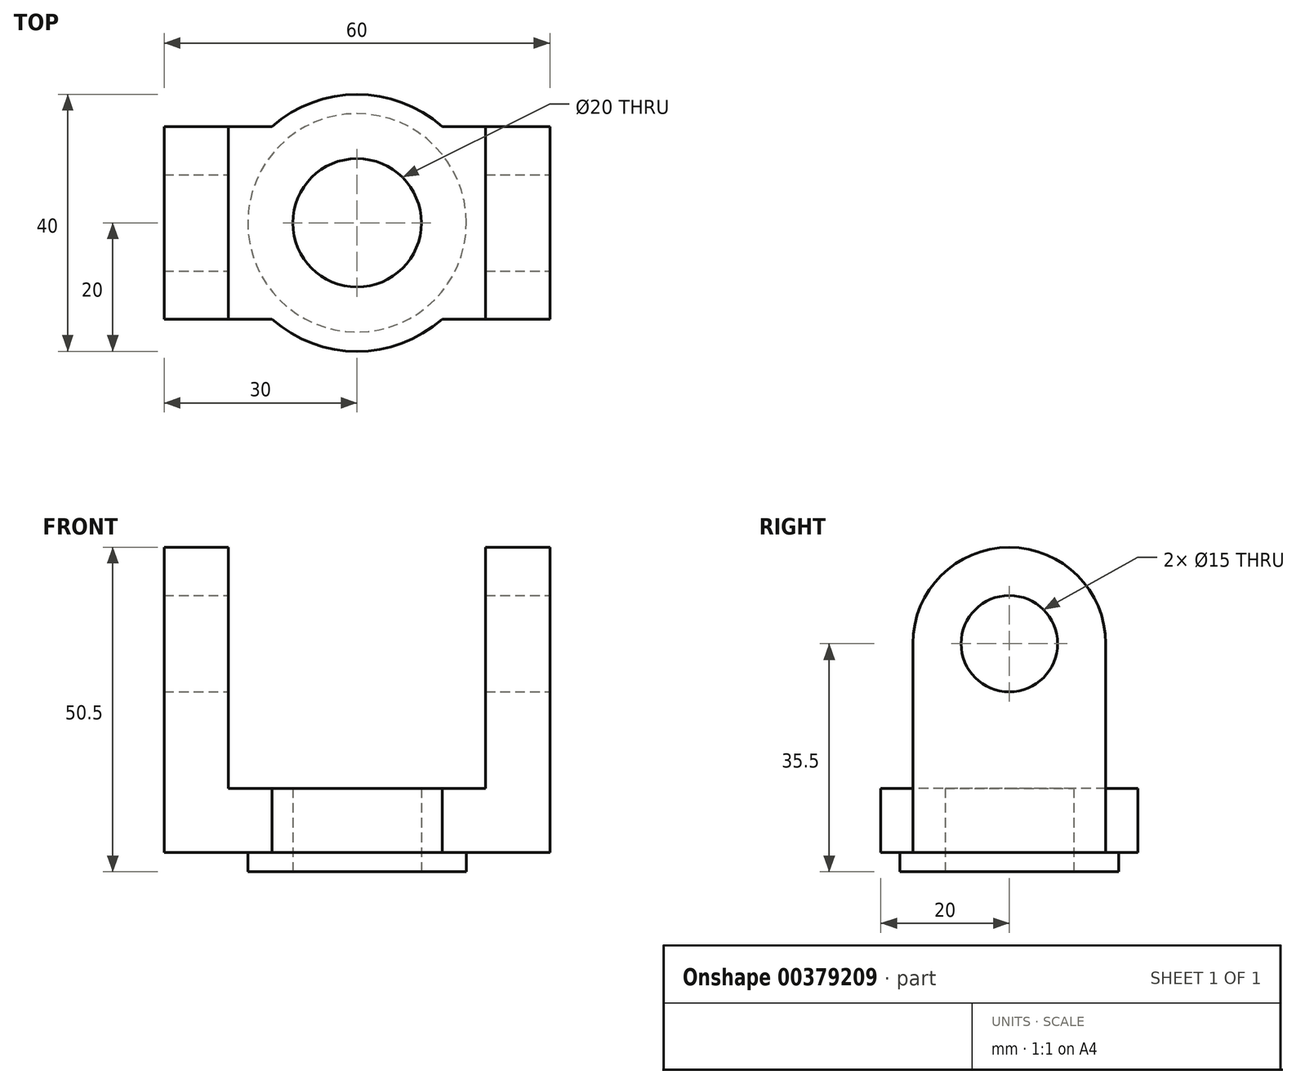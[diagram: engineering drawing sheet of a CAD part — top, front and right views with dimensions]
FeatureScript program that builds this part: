
annotation { "Feature Type Name" : "Feature", "Feature Type Description" : "" }
export const myFeature = defineFeature(function(context is Context, id is Id, definition is map)
    precondition{}
    {
        {
            var Q0;
            Q0=qCreatedBy(makeId("Top.planeOp"),FACE);
            var sketch = newSketch(context, id + "F0", { "sketchPlane" : qUnion([Q0])});
            skLineSegment(sketch, "E0", {"start": v(0, 0) * mm, "end": v(60, 0) * mm});
            skLineSegment(sketch, "E1", {"start": v(60, 0) * mm, "end": v(60, 30) * mm});
            skLineSegment(sketch, "E2", {"start": v(60, 30) * mm, "end": v(0, 30) * mm});
            skLineSegment(sketch, "E3", {"start": v(0, 30) * mm, "end": v(0, 0) * mm});
            skLineSegment(sketch, "E4", {"start": v(0, 15) * mm, "end": v(10, 15) * mm});
            skLineSegment(sketch, "E5", {"start": v(60, 15) * mm, "end": v(49.27, 20.37) * mm});
            skArc(sketch, "E6", {"start": v(43.23, 30) * mm, "mid": v(30, 35) * mm, "end": v(16.77, 30) * mm});
            skPoint(sketch, "E7.orphan", {"position": v(30, 30) * mm});
            skLineSegment(sketch, "E8.trimOffspring", {"start": v(50, 15) * mm, "end": v(60, 15) * mm});
            skPoint(sketch, "E9.end.orphan", {"position": v(30, 0) * mm});
            skArc(sketch, "E10.trimOffspring", {"start": v(16.77, 0) * mm, "mid": v(30, -5) * mm, "end": v(43.23, 0) * mm});
            skArc(sketch, "E11.trimOffspring", {"start": v(50, 15) * mm, "mid": v(49.82, 17.7) * mm, "end": v(49.27, 20.37) * mm});
            skSolve(sketch);
        }
        {
            var Q0;
            Q0 = qSketchRegion(id + "F0", true);
            extrude(context, id + "F1", {"entities" : qUnion([Q0]), "depth" : 47.5 * mm});
        }
        {
            var Q0;
            {var subQ0=sQuery(id+"F0.wireOp",EDGE,"E0");Q0=makeQuery(id+"F1.opExtrude","SWEPT_FACE",FACE,{"disambiguationData":[OSD([subQ0]),TDD([makeQuery(id+"F0.imprint","IMPRINT",EDGE,{"disambiguationData":[TD([[makeQuery(id+"F0.imprint","INTERSECT",VERTEX,{"derivedFrom":[subQ0,sQuery(id+"F0.wireOp",EDGE,"E3")]}),-1.0]])],"derivedFrom":subQ0})])]});}
            var sketch = newSketch(context, id + "F2", { "sketchPlane" : qUnion([Q0])});
            skLineSegment(sketch, "E12", {"start": v(0, 47.5) * mm, "end": v(10, 47.5) * mm});
            skLineSegment(sketch, "E13", {"start": v(10, 47.5) * mm, "end": v(10, 10) * mm});
            skLineSegment(sketch, "E14", {"start": v(10, 10) * mm, "end": v(50, 10) * mm});
            skLineSegment(sketch, "E15", {"start": v(50, 10) * mm, "end": v(50, 47.5) * mm});
            skLineSegment(sketch, "E16", {"start": v(50, 47.5) * mm, "end": v(10, 47.5) * mm});
            skSolve(sketch);
        }
        {
            var Q0;
            Q0 = qSketchRegion(id + "F2", true);
            extrude(context, id + "F3", {"entities" : qUnion([Q0]), "operationType" : NewBodyOperationType.REMOVE, "oppositeDirection" : true, "depth" : 205 * mm});
        }
        {
            var Q0;
            Q0=makeQuery(id+"F3.boolean.opBoolean","COPY",FACE,{"derivedFrom":makeQuery(id+"F3.opExtrude","CAP_FACE",FACE,{"disambiguationData":[OSD([sQuery(id+"F2.wireOp",EDGE,"E13"),sQuery(id+"F2.wireOp",EDGE,"E14"),sQuery(id+"F2.wireOp",EDGE,"E15"),sQuery(id+"F2.wireOp",EDGE,"E16")])],"isStart":true})});
            var sketch = newSketch(context, id + "F4", { "sketchPlane" : qUnion([Q0])});
            skLineSegment(sketch, "E17", {"start": v(-43.23, 47.5) * mm, "end": v(-16.77, 47.5) * mm});
            skLineSegment(sketch, "E18", {"start": v(-16.77, 47.5) * mm, "end": v(-16.77, 10) * mm});
            skLineSegment(sketch, "E19", {"start": v(-16.77, 10) * mm, "end": v(-43.23, 10) * mm});
            skLineSegment(sketch, "E20", {"start": v(-43.23, 10) * mm, "end": v(-43.23, 47.5) * mm});
            skSolve(sketch);
        }
        {
            var Q0;
            Q0 = qSketchRegion(id + "F4", true);
            extrude(context, id + "F5", {"entities" : qUnion([Q0]), "operationType" : NewBodyOperationType.REMOVE, "oppositeDirection" : true, "depth" : 25 * mm});
        }
        {
            var Q0;
            Q0=makeQuery(id+"F1.opExtrude","CAP_FACE",FACE,{"disambiguationData":[OSD([sQuery(id+"F0.wireOp",EDGE,"E0"),sQuery(id+"F0.wireOp",EDGE,"E1"),sQuery(id+"F0.wireOp",EDGE,"E2"),sQuery(id+"F0.wireOp",EDGE,"E3"),sQuery(id+"F0.wireOp",EDGE,"E6"),sQuery(id+"F0.wireOp",EDGE,"E10.trimOffspring")])],"isStart":true});
            var sketch = newSketch(context, id + "F6", { "sketchPlane" : qUnion([Q0])});
            skCircle(sketch, "E21", {"center": v(30, -15) * mm, "radius": 17 * mm});
            skSolve(sketch);
        }
        {
            var Q0;
            Q0 = qSketchRegion(id + "F6", true);
            extrude(context, id + "F7", {"entities" : qUnion([Q0]), "operationType" : NewBodyOperationType.ADD, "depth" : 3 * mm});
        }
        {
            var Q0;
            Q0=makeQuery(id+"F7.opExtrude","CAP_FACE",FACE,{"disambiguationData":[OSD([sQuery(id+"F6.wireOp",EDGE,"E21")])],"isStart":false});
            var sketch = newSketch(context, id + "F8", { "sketchPlane" : qUnion([Q0])});
            skCircle(sketch, "E22", {"center": v(30, -15) * mm, "radius": 10 * mm});
            skSolve(sketch);
        }
        {
            var Q0;
            Q0 = qSketchRegion(id + "F8", true);
            extrude(context, id + "F9", {"entities" : qUnion([Q0]), "operationType" : NewBodyOperationType.REMOVE, "oppositeDirection" : true, "depth" : 25 * mm});
        }
        {
            var Q0;
            Q0=makeQuery(id+"F1.opExtrude","SWEPT_FACE",FACE,{"disambiguationData":[OSD([sQuery(id+"F0.wireOp",EDGE,"E1")])]});
            var sketch = newSketch(context, id + "F10", { "sketchPlane" : qUnion([Q0])});
            skLineSegment(sketch, "E23", {"start": v(15, 0) * mm, "end": v(15, 32.5) * mm});
            skCircle(sketch, "E24", {"center": v(15, 32.5) * mm, "radius": 7.5 * mm});
            skSolve(sketch);
        }
        {
            var Q0;
            Q0 = qSketchRegion(id + "F10", true);
            extrude(context, id + "F11", {"entities" : qUnion([Q0]), "operationType" : NewBodyOperationType.REMOVE, "oppositeDirection" : true, "depth" : 125 * mm});
        }
        {
            var Q0;
            {var subQ0=sQuery(id+"F0.wireOp",EDGE,"E0");Q0=makeQuery(id+"F1.opExtrude","CAP_EDGE",EDGE,{"disambiguationData":[OSD([subQ0]),TDD([makeQuery(id+"F0.imprint","IMPRINT",EDGE,{"disambiguationData":[TD([[makeQuery(id+"F0.imprint","INTERSECT",VERTEX,{"derivedFrom":[subQ0,sQuery(id+"F0.wireOp",EDGE,"E1")]}),1.0]])],"derivedFrom":subQ0})])],"isStart":false});}
            var Q1;
            {var subQ0=sQuery(id+"F0.wireOp",EDGE,"E2");Q1=makeQuery(id+"F1.opExtrude","CAP_EDGE",EDGE,{"disambiguationData":[OSD([subQ0]),TDD([makeQuery(id+"F0.imprint","IMPRINT",EDGE,{"disambiguationData":[TD([[makeQuery(id+"F0.imprint","INTERSECT",VERTEX,{"derivedFrom":[sQuery(id+"F0.wireOp",EDGE,"E1"),subQ0]}),-1.0]])],"derivedFrom":subQ0})])],"isStart":false});}
            var Q2;
            {var subQ0=sQuery(id+"F0.wireOp",EDGE,"E0");Q2=makeQuery(id+"F1.opExtrude","CAP_EDGE",EDGE,{"disambiguationData":[OSD([subQ0]),TDD([makeQuery(id+"F0.imprint","IMPRINT",EDGE,{"disambiguationData":[TD([[makeQuery(id+"F0.imprint","INTERSECT",VERTEX,{"derivedFrom":[subQ0,sQuery(id+"F0.wireOp",EDGE,"E3")]}),-1.0]])],"derivedFrom":subQ0})])],"isStart":false});}
            var Q3;
            {var subQ0=sQuery(id+"F0.wireOp",EDGE,"E2");Q3=makeQuery(id+"F1.opExtrude","CAP_EDGE",EDGE,{"disambiguationData":[OSD([subQ0]),TDD([makeQuery(id+"F0.imprint","IMPRINT",EDGE,{"disambiguationData":[TD([[makeQuery(id+"F0.imprint","INTERSECT",VERTEX,{"derivedFrom":[subQ0,sQuery(id+"F0.wireOp",EDGE,"E3")]}),1.0]])],"derivedFrom":subQ0})])],"isStart":false});}
            fillet(context, id + "F12", {"entities" : qUnion([Q0, Q1, Q2, Q3]), "radius" : 15 * mm, "tangentPropagation" : true, "allowEdgeOverflow" : false});
        }
    });
